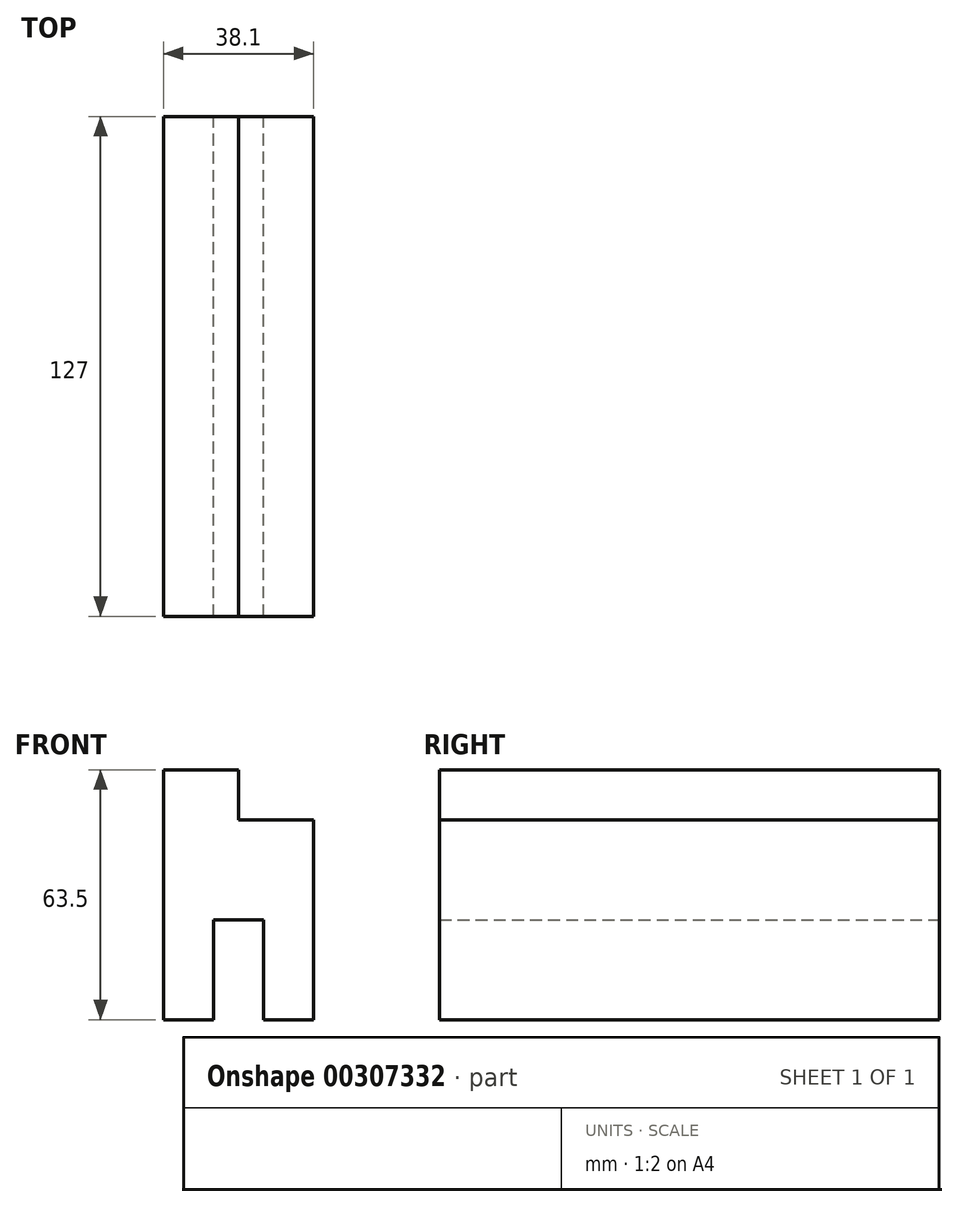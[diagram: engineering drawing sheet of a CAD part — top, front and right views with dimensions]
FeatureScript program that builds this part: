
annotation { "Feature Type Name" : "Feature", "Feature Type Description" : "" }
export const myFeature = defineFeature(function(context is Context, id is Id, definition is map)
    precondition{}
    {
        {
            var Q0;
            Q0=qCreatedBy(makeId("Front.planeOp"),FACE);
            var sketch = newSketch(context, id + "F0", { "sketchPlane" : qUnion([Q0])});
            skLineSegment(sketch, "E0", {"start": v(-59.05, -13.7) * mm, "end": v(-46.35, -13.7) * mm});
            skLineSegment(sketch, "E1", {"start": v(-46.35, -13.7) * mm, "end": v(-46.35, 11.7) * mm});
            skLineSegment(sketch, "E2", {"start": v(-46.35, 11.7) * mm, "end": v(-33.65, 11.7) * mm});
            skLineSegment(sketch, "E3", {"start": v(-33.65, 11.7) * mm, "end": v(-33.65, -13.7) * mm});
            skLineSegment(sketch, "E4", {"start": v(-33.65, -13.7) * mm, "end": v(-20.95, -13.7) * mm});
            skLineSegment(sketch, "E5", {"start": v(-20.95, -13.7) * mm, "end": v(-20.95, 37.1) * mm});
            skLineSegment(sketch, "E6", {"start": v(-40, 49.8) * mm, "end": v(-59.05, 49.8) * mm});
            skLineSegment(sketch, "E7", {"start": v(-59.05, 49.8) * mm, "end": v(-59.05, -13.7) * mm});
            skPoint(sketch, "E8.end.orphan", {"position": v(-46.35, 27.46) * mm});
            skLineSegment(sketch, "E9", {"start": v(-40, 49.8) * mm, "end": v(-40, 37.1) * mm});
            skLineSegment(sketch, "E10", {"start": v(-40, 37.1) * mm, "end": v(-20.95, 37.1) * mm});
            skSolve(sketch);
        }
        {
            var Q0;
            Q0 = qSketchRegion(id + "F0", true);
            extrude(context, id + "F1", {"entities" : qUnion([Q0]), "depth" : 127 * mm});
        }
    });
